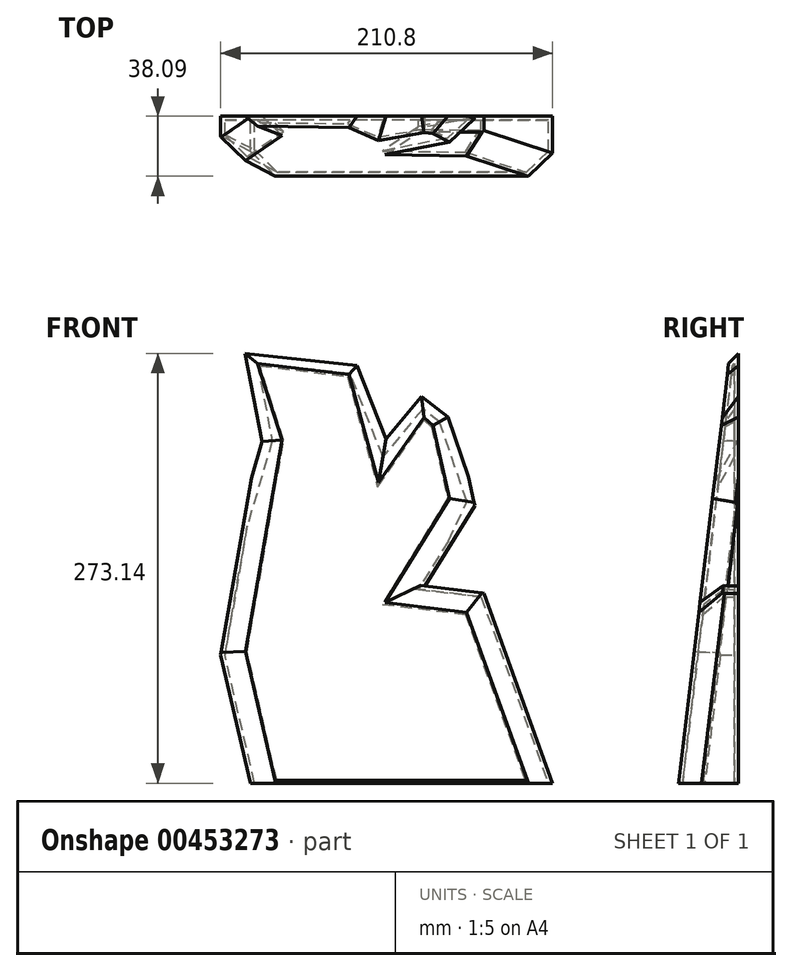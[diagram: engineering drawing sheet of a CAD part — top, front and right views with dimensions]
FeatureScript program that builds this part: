
annotation { "Feature Type Name" : "Feature", "Feature Type Description" : "" }
export const myFeature = defineFeature(function(context is Context, id is Id, definition is map)
    precondition{}
    {
        {
            var Q0;
            Q0=qCreatedBy(makeId("Front.planeOp"),FACE);
            var sketch = newSketch(context, id + "F0", { "sketchPlane" : qUnion([Q0])});
            skLineSegment(sketch, "E0", {"start": v(-50.3, -70.68) * mm, "end": v(-69.15, 10.73) * mm});
            skLineSegment(sketch, "E1", {"start": v(-69.15, 10.73) * mm, "end": v(-46, 144.42) * mm});
            skLineSegment(sketch, "E2", {"start": v(-46, 144.42) * mm, "end": v(-67.43, 212.12) * mm});
            skLineSegment(sketch, "E3", {"start": v(-67.43, 212.12) * mm, "end": v(24.26, 200.98) * mm});
            skLineSegment(sketch, "E4", {"start": v(24.26, 200.98) * mm, "end": v(37.03, 153.95) * mm});
            skLineSegment(sketch, "E5", {"start": v(37.03, 153.95) * mm, "end": v(57.17, 182.84) * mm});
            skLineSegment(sketch, "E6", {"start": v(57.17, 182.84) * mm, "end": v(79.49, 162.7) * mm});
            skLineSegment(sketch, "E7", {"start": v(79.49, 162.7) * mm, "end": v(92.18, 105.8) * mm});
            skLineSegment(sketch, "E8", {"start": v(92.18, 105.8) * mm, "end": v(60.67, 54.59) * mm});
            skLineSegment(sketch, "E9", {"start": v(60.67, 54.59) * mm, "end": v(98.01, 50.05) * mm});
            skLineSegment(sketch, "E10", {"start": v(98.01, 50.05) * mm, "end": v(141.65, -70.68) * mm});
            skLineSegment(sketch, "E11", {"start": v(141.65, -70.68) * mm, "end": v(-50.3, -70.68) * mm});
            skSolve(sketch);
        }
        {
            var Q0;
            Q0=makeQuery(id+"F0.imprint","IMPRINT",FACE,{"disambiguationData":[TD([[makeQuery(id+"F0.imprint","IMPRINT",EDGE,{"derivedFrom":sQuery(id+"F0.wireOp",EDGE,"E0")}),-1.0]])]});
            extrude(context, id + "F1", {"entities" : qUnion([Q0]), "depth" : 38.1 * mm});
        }
        {
            var Q0;
            Q0=qCreatedBy(makeId("Right.planeOp"),FACE);
            cPlane(context, id + "F2", {"entities" : qUnion([Q0]), "cplaneType" : CPlaneType.OFFSET, "offset" : 76.2 * mm, "oppositeDirection" : true, "width" : 152.4 * mm, "height" : 152.4 * mm});
        }
        {
            var Q0;
            Q0=qCreatedBy(id+"F2.planeOp",FACE);
            var sketch = newSketch(context, id + "F3", { "sketchPlane" : qUnion([Q0])});
            skLineSegment(sketch, "E12", {"start": v(-38.19, -70.6) * mm, "end": v(0, 248.97) * mm});
            skLineSegment(sketch, "E13", {"start": v(0, 248.97) * mm, "end": v(-45.77, 254.44) * mm});
            skLineSegment(sketch, "E14", {"start": v(-45.77, 254.44) * mm, "end": v(-38.19, -70.6) * mm});
            skSolve(sketch);
        }
        {
            var Q0;
            Q0 = qSketchRegion(id + "F3", true);
            extrude(context, id + "F4", {"entities" : qUnion([Q0]), "operationType" : NewBodyOperationType.REMOVE, "endBound" : BoundingType.THROUGH_ALL, "depth" : 25.4 * mm});
        }
        {
            var Q0;
            Q0=makeQuery(id+"F4.boolean.opBoolean","COPY",FACE,{"derivedFrom":makeQuery(id+"F4.opExtrude","SWEPT_FACE",FACE,{"disambiguationData":[OSD([sQuery(id+"F3.wireOp",EDGE,"E12")])]})});
            chamfer(context, id + "F5", {"entities" : qUnion([Q0]), "width" : 15.24 * mm, "tangentPropagation" : true});
        }
        {
            var Q0;
            Q0=makeQuery(id+"F1.opExtrude","SWEPT_FACE",FACE,{"disambiguationData":[OSD([sQuery(id+"F0.wireOp",EDGE,"5UBScBti-lYJG-QWJU-C9wr-LBJ0cxTIyK4E")])]});
            var Q1;
            Q1=makeQuery(id+"F1.opExtrude","SWEPT_FACE",FACE,{"disambiguationData":[OSD([sQuery(id+"F0.wireOp",EDGE,"E11")])]});
            shell(context, id + "F6", {"entities" : qUnion([Q0, Q1]), "thickness" : 2.54 * mm});
        }
    });
